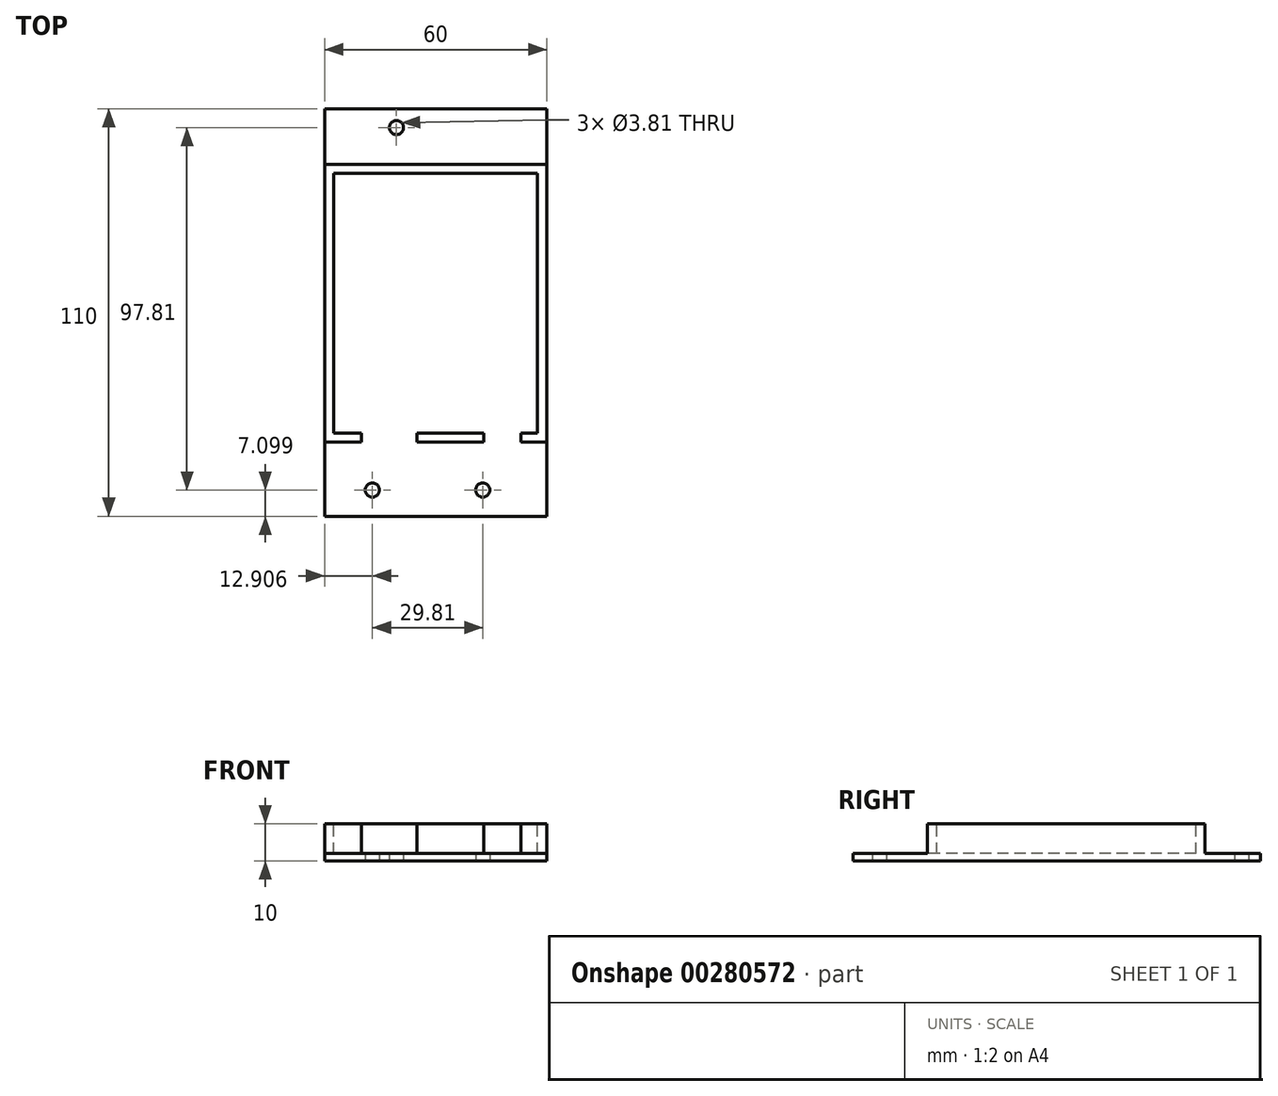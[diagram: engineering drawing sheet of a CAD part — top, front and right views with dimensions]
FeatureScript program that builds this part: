
annotation { "Feature Type Name" : "Feature", "Feature Type Description" : "" }
export const myFeature = defineFeature(function(context is Context, id is Id, definition is map)
    precondition{}
    {
        {
            var Q0;
            Q0=qCreatedBy(makeId("Top.planeOp"),FACE);
            var sketch = newSketch(context, id + "F0", { "sketchPlane" : qUnion([Q0])});
            skLineSegment(sketch, "E0.bottom", {"start": v(-31.78, -37.22) * mm, "end": v(28.22, -37.22) * mm});
            skLineSegment(sketch, "E0.top", {"start": v(-31.78, 37.78) * mm, "end": v(28.22, 37.78) * mm});
            skLineSegment(sketch, "E0.left", {"start": v(-31.78, -37.22) * mm, "end": v(-31.78, 37.78) * mm});
            skLineSegment(sketch, "E0.right", {"start": v(28.22, -37.22) * mm, "end": v(28.22, 37.78) * mm});
            skSolve(sketch);
        }
        {
            var Q0;
            Q0=makeQuery(id+"F0.imprint","IMPRINT",FACE,{"disambiguationData":[TD([[makeQuery(id+"F0.imprint","IMPRINT",EDGE,{"derivedFrom":sQuery(id+"F0.wireOp",EDGE,"E0.bottom")}),1.0]])]});
            extrude(context, id + "F1", {"entities" : qUnion([Q0]), "depth" : 10 * mm});
        }
        {
            var Q0;
            Q0=makeQuery(id+"F1.opExtrude","CAP_FACE",FACE,{"disambiguationData":[OSD([sQuery(id+"F0.wireOp",EDGE,"E0.bottom"),sQuery(id+"F0.wireOp",EDGE,"E0.top"),sQuery(id+"F0.wireOp",EDGE,"E0.left"),sQuery(id+"F0.wireOp",EDGE,"E0.right")])],"isStart":false});
            var sketch = newSketch(context, id + "F2", { "sketchPlane" : qUnion([Q0])});
            skLineSegment(sketch, "E1.bottom", {"start": v(-29.28, 35.28) * mm, "end": v(25.72, 35.28) * mm});
            skLineSegment(sketch, "E1.top", {"start": v(-29.28, -34.72) * mm, "end": v(25.72, -34.72) * mm});
            skLineSegment(sketch, "E1.left", {"start": v(-29.28, 35.28) * mm, "end": v(-29.28, -34.72) * mm});
            skLineSegment(sketch, "E1.right", {"start": v(25.72, 35.28) * mm, "end": v(25.72, -34.72) * mm});
            skSolve(sketch);
        }
        {
            var Q0;
            Q0 = qSketchRegion(id + "F2", true);
            extrude(context, id + "F3", {"entities" : qUnion([Q0]), "operationType" : NewBodyOperationType.REMOVE, "oppositeDirection" : true, "depth" : 8 * mm});
        }
        {
            var Q0;
            Q0=makeQuery(id+"F3.boolean.opBoolean","COPY",FACE,{"derivedFrom":makeQuery(id+"F3.opExtrude","CAP_FACE",FACE,{"disambiguationData":[OSD([sQuery(id+"F2.wireOp",EDGE,"E1.bottom"),sQuery(id+"F2.wireOp",EDGE,"E1.top"),sQuery(id+"F2.wireOp",EDGE,"E1.left"),sQuery(id+"F2.wireOp",EDGE,"E1.right")])],"isStart":false})});
            var sketch = newSketch(context, id + "F4", { "sketchPlane" : qUnion([Q0])});
            skLineSegment(sketch, "E2.bottom", {"start": v(-21.78, -34.48) * mm, "end": v(-6.78, -34.48) * mm});
            skLineSegment(sketch, "E2.top", {"start": v(-21.78, -37.6) * mm, "end": v(-6.78, -37.6) * mm});
            skLineSegment(sketch, "E2.left", {"start": v(-21.78, -34.48) * mm, "end": v(-21.78, -37.6) * mm});
            skLineSegment(sketch, "E2.right", {"start": v(-6.78, -34.48) * mm, "end": v(-6.78, -37.6) * mm});
            skLineSegment(sketch, "E3.bottom", {"start": v(11.22, -34.48) * mm, "end": v(21.22, -34.48) * mm});
            skLineSegment(sketch, "E3.top", {"start": v(11.22, -37.6) * mm, "end": v(21.22, -37.6) * mm});
            skLineSegment(sketch, "E3.left", {"start": v(11.22, -34.48) * mm, "end": v(11.22, -37.6) * mm});
            skLineSegment(sketch, "E3.right", {"start": v(21.22, -34.48) * mm, "end": v(21.22, -37.6) * mm});
            skSolve(sketch);
        }
        {
            var Q0;
            Q0 = qSketchRegion(id + "F4", true);
            extrude(context, id + "F5", {"entities" : qUnion([Q0]), "operationType" : NewBodyOperationType.REMOVE, "depth" : 8 * mm});
        }
        {
            var Q0;
            Q0=qCreatedBy(makeId("Top.planeOp"),FACE);
            var sketch = newSketch(context, id + "F6", { "sketchPlane" : qUnion([Q0])});
            skLineSegment(sketch, "E4.bottom", {"start": v(-31.78, -37.22) * mm, "end": v(28.22, -37.22) * mm});
            skLineSegment(sketch, "E4.top", {"start": v(-31.78, -57.22) * mm, "end": v(28.22, -57.22) * mm});
            skLineSegment(sketch, "E4.left", {"start": v(-31.78, -37.22) * mm, "end": v(-31.78, -57.22) * mm});
            skLineSegment(sketch, "E4.right", {"start": v(28.22, -37.22) * mm, "end": v(28.22, -57.22) * mm});
            skCircle(sketch, "E5", {"center": v(-18.87, -50.12) * mm, "radius": 1.9 * mm});
            skCircle(sketch, "E6", {"center": v(10.94, -50.12) * mm, "radius": 1.9 * mm});
            skSolve(sketch);
        }
        {
            var Q0;
            Q0 = qSketchRegion(id + "F6", true);
            extrude(context, id + "F7", {"entities" : qUnion([Q0]), "operationType" : NewBodyOperationType.ADD, "depth" : 2 * mm});
        }
        {
            var Q0;
            Q0=qCreatedBy(makeId("Top.planeOp"),FACE);
            var sketch = newSketch(context, id + "F8", { "sketchPlane" : qUnion([Q0])});
            skLineSegment(sketch, "E7.bottom", {"start": v(-31.78, 37.78) * mm, "end": v(28.22, 37.78) * mm});
            skLineSegment(sketch, "E7.top", {"start": v(-31.78, 52.78) * mm, "end": v(28.22, 52.78) * mm});
            skLineSegment(sketch, "E7.left", {"start": v(-31.78, 37.78) * mm, "end": v(-31.78, 52.78) * mm});
            skLineSegment(sketch, "E7.right", {"start": v(28.22, 37.78) * mm, "end": v(28.22, 52.78) * mm});
            skCircle(sketch, "E8", {"center": v(-12.37, 47.69) * mm, "radius": 1.9 * mm});
            skSolve(sketch);
        }
        {
            var Q0;
            Q0 = qSketchRegion(id + "F8", true);
            extrude(context, id + "F9", {"entities" : qUnion([Q0]), "operationType" : NewBodyOperationType.ADD, "depth" : 2 * mm});
        }
    });
